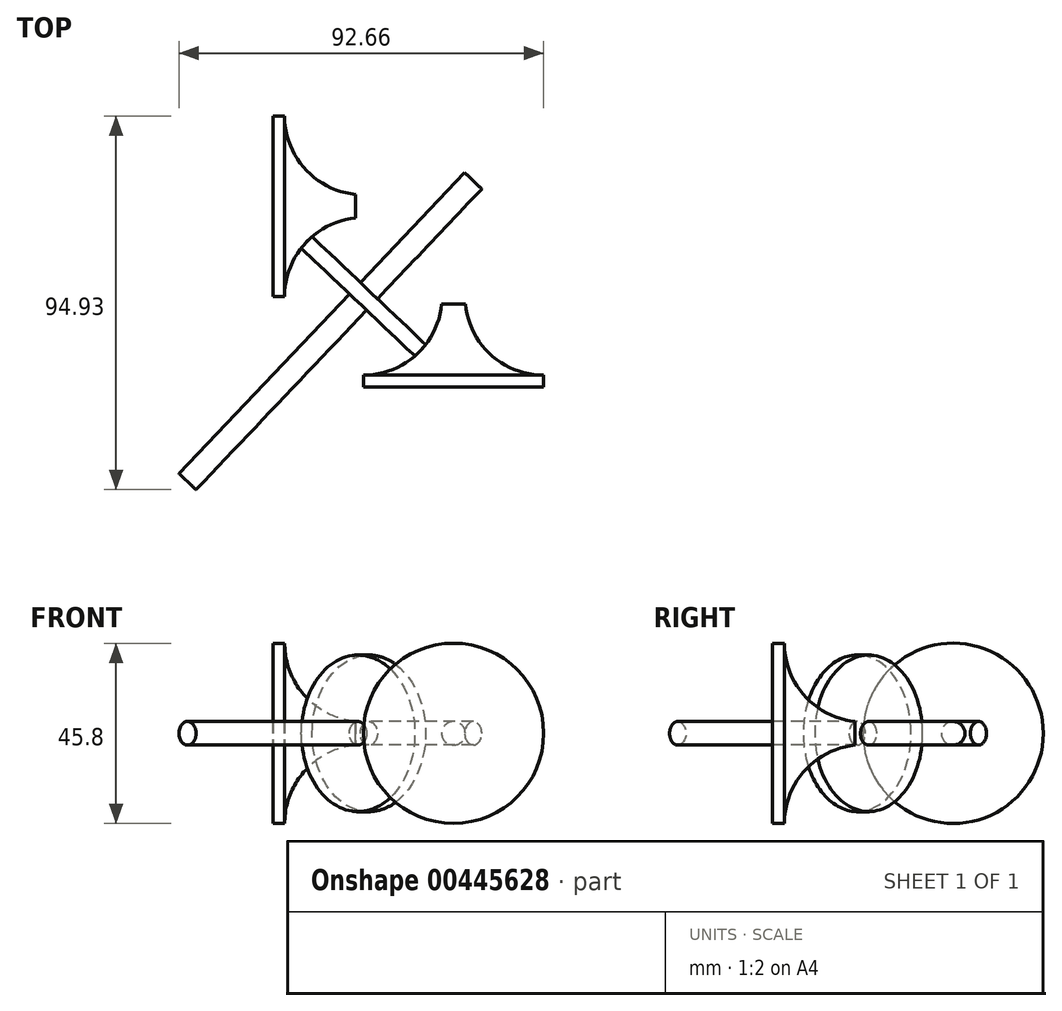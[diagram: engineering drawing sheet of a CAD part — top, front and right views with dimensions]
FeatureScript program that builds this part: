
annotation { "Feature Type Name" : "Feature", "Feature Type Description" : "" }
export const myFeature = defineFeature(function(context is Context, id is Id, definition is map)
    precondition{}
    {
        {
            var Q0;
            Q0=qCreatedBy(makeId("Top.planeOp"),FACE);
            var sketch = newSketch(context, id + "F0", { "sketchPlane" : qUnion([Q0])});
            skLineSegment(sketch, "E0.bottom", {"start": v(25, -25) * mm, "end": v(-25, -25) * mm});
            skLineSegment(sketch, "E0.top", {"start": v(25, 25) * mm, "end": v(-25, 25) * mm});
            skLineSegment(sketch, "E0.left", {"start": v(25, 2) * mm, "end": v(25, 5) * mm});
            skLineSegment(sketch, "E0.right", {"start": v(-25, -25) * mm, "end": v(-25, 25) * mm});
            skPoint(sketch, "E0.middle", {"position": v(0, 0) * mm});
            skArc(sketch, "E1", {"start": v(25, 45) * mm, "mid": v(10.86, 39.14) * mm, "end": v(5, 25) * mm});
            skLineSegment(sketch, "E2", {"start": v(25, 25) * mm, "end": v(25, 63.82) * mm});
            skLineSegment(sketch, "E3", {"start": v(25, 25) * mm, "end": v(23, 25) * mm});
            skLineSegment(sketch, "E4", {"start": v(23, 25) * mm, "end": v(23, 57.85) * mm});
            skLineSegment(sketch, "E5", {"start": v(44.9, 23) * mm, "end": v(47.9, 23) * mm});
            skPoint(sketch, "E5.startSnap0", {"position": v(44.22, 23) * mm});
            skLineSegment(sketch, "E6", {"start": v(25, 5) * mm, "end": v(25, 2) * mm});
            skLineSegment(sketch, "E7", {"start": v(25, 2) * mm, "end": v(47.9, 2) * mm});
            skLineSegment(sketch, "E8.MirrorCS", {"start": v(47.9, 2) * mm, "end": v(41.64, 2) * mm});
            skLineSegment(sketch, "E9", {"start": v(47.9, 2) * mm, "end": v(44.9, 2) * mm});
            skLineSegment(sketch, "E10", {"start": v(44.9, 2) * mm, "end": v(44.9, -38) * mm});
            skLineSegment(sketch, "E11.top", {"start": v(47.9, -38) * mm, "end": v(44.9, -38) * mm});
            skLineSegment(sketch, "E12", {"start": v(47.9, 23) * mm, "end": v(47.9, -38) * mm});
            skPoint(sketch, "E13.orphan", {"position": v(50.9, -38) * mm});
            skArc(sketch, "E14.trimOffspring", {"start": v(25, 5) * mm, "mid": v(38.42, 10.17) * mm, "end": v(44.9, 23) * mm});
            skLineSegment(sketch, "E15", {"start": v(23, 44.9) * mm, "end": v(47.9, 44.9) * mm});
            skSolve(sketch);
        }
        {
            var Q0;
            {var subQ0=sQuery(id+"F0.wireOp",EDGE,"E5");Q0=makeQuery(id+"F0.imprint","IMPRINT",FACE,{"disambiguationData":[TD([[makeQuery(id+"F0.imprint","IMPRINT",EDGE,{"derivedFrom":subQ0}),-1.0]])]});}
            var Q1;
            {var subQ0=sQuery(id+"F0.wireOp",EDGE,"E9");Q1=makeQuery(id+"F0.imprint","IMPRINT",FACE,{"disambiguationData":[TD([[makeQuery(id+"F0.imprint","IMPRINT",EDGE,{"derivedFrom":subQ0}),1.0]])]});}
            var Q2;
            Q2=sQuery(id+"F0.wireOp",EDGE,"E12");
            revolve(context, id + "F1", {"entities" : qUnion([Q0, Q1]), "axis" : qUnion([Q2]), "revolveType" : RevolveType.FULL});
        }
        {
            var Q0;
            Q0=sQuery(id+"F0.wireOp",VERTEX,"E15.end");
            var Q1;
            Q1=sQuery(id+"F0.wireOp",EDGE,"E15");
            cPlane(context, id + "F2", {"entities" : qUnion([Q0, Q1]), "cplaneType" : CPlaneType.LINE_POINT, "offset" : 25 * mm, "width" : 150 * mm, "height" : 150 * mm});
        }
        {
            var Q0;
            Q0=qCreatedBy(id+"F2.planeOp",FACE);
            var sketch = newSketch(context, id + "F3", { "sketchPlane" : qUnion([Q0])});
            skPoint(sketch, "E16.0", {"position": v(44.9, 0) * mm});
            skLineSegment(sketch, "E17", {"start": v(44.9, 0) * mm, "end": v(44.9, 42.47) * mm});
            skSolve(sketch);
        }
        {
            var Q0;
            Q0=makeQuery(id+"F1.opRevolve","SWEPT_BODY",BODY,{"disambiguationData":[OSD([sQuery(id+"F0.wireOp",EDGE,"E5"),sQuery(id+"F0.wireOp",EDGE,"E6"),sQuery(id+"F0.wireOp",EDGE,"E7"),sQuery(id+"F0.wireOp",EDGE,"E8.MirrorCS"),sQuery(id+"F0.wireOp",EDGE,"E11.top"),sQuery(id+"F0.wireOp",EDGE,"E10"),sQuery(id+"F0.wireOp",EDGE,"E12"),sQuery(id+"F0.wireOp",EDGE,"E14.trimOffspring")])]});
            var Q1;
            Q1=sQuery(id+"F3.wireOp",EDGE,"E17");
            circularPattern(context, id + "F4", {"entities" : qUnion([Q0]), "axis" : qUnion([Q1]), "angle" : 270 * degree, "instanceCount" : 2, "equalSpace" : true});
        }
        {
            var Q0;
            Q0=makeQuery(id+"F4.opPattern","COPY",BODY,{"derivedFrom":makeQuery(id+"F1.opRevolve","SWEPT_BODY",BODY,{"disambiguationData":[OSD([sQuery(id+"F0.wireOp",EDGE,"E5"),sQuery(id+"F0.wireOp",EDGE,"E6"),sQuery(id+"F0.wireOp",EDGE,"E7"),sQuery(id+"F0.wireOp",EDGE,"E8.MirrorCS"),sQuery(id+"F0.wireOp",EDGE,"E11.top"),sQuery(id+"F0.wireOp",EDGE,"E10"),sQuery(id+"F0.wireOp",EDGE,"E12"),sQuery(id+"F0.wireOp",EDGE,"E14.trimOffspring")])]}),"instanceName":"1"});
            transform(context, id + "F5", {"entities" : qUnion([Q0]), "transformType" : TransformType.TRANSLATION_3D, "dx" : -3 * mm, "dy" : 3 * mm, "dz" : 0 * mm, "makeCopy" : false});
        }
        {
            var Q0;
            Q0=qCreatedBy(makeId("Top.planeOp"),FACE);
            var sketch = newSketch(context, id + "F6", { "sketchPlane" : qUnion([Q0])});
            skLineSegment(sketch, "E18", {"start": v(10.33, 36.18) * mm, "end": v(9.23, 37.22) * mm});
            skLineSegment(sketch, "E19", {"start": v(10.33, 36.18) * mm, "end": v(23.64, 23.53) * mm});
            skArc(sketch, "E20", {"start": v(11.99, 40.12) * mm, "mid": v(10.54, 38.74) * mm, "end": v(9.23, 37.22) * mm});
            skLineSegment(sketch, "E21", {"start": v(26.4, 26.43) * mm, "end": v(23.64, 23.53) * mm});
            skLineSegment(sketch, "E22.trimOffspring", {"start": v(26.4, 26.43) * mm, "end": v(11.99, 40.12) * mm});
            skSolve(sketch);
        }
        {
            var Q0;
            Q0=makeQuery(id+"F6.imprint","IMPRINT",FACE,{"disambiguationData":[TD([[makeQuery(id+"F6.imprint","IMPRINT",EDGE,{"derivedFrom":sQuery(id+"F6.wireOp",EDGE,"E18")}),-1.0]])]});
            var Q1;
            Q1=sQuery(id+"F6.wireOp",EDGE,"E21");
            revolve(context, id + "F7", {"entities" : qUnion([Q0]), "axis" : qUnion([Q1]), "revolveType" : RevolveType.FULL});
        }
        {
            var Q0;
            Q0=makeQuery(id+"F7.opRevolve","SWEPT_FACE",FACE,{"disambiguationData":[OSD([sQuery(id+"F6.wireOp",EDGE,"E18"),sQuery(id+"F6.wireOp",EDGE,"E19")])]});
            var sketch = newSketch(context, id + "F8", { "sketchPlane" : qUnion([Q0])});
            skCircle(sketch, "E23", {"center": v(0.93, 0) * mm, "radius": 3 * mm});
            skSolve(sketch);
        }
        {
            var Q0;
            Q0=makeQuery(id+"F8.imprint","IMPRINT",FACE,{"disambiguationData":[TD([[makeQuery(id+"F8.imprint","IMPRINT",EDGE,{"derivedFrom":sQuery(id+"F8.wireOp",EDGE,"E23")}),1.0]])]});
            extrude(context, id + "F9", {"entities" : qUnion([Q0]), "operationType" : NewBodyOperationType.ADD, "oppositeDirection" : true, "depth" : 42.5 * mm, "hasSecondDirection" : true, "secondDirectionOppositeDirection" : false, "secondDirectionDepth" : 62.9 * mm});
        }
    });
